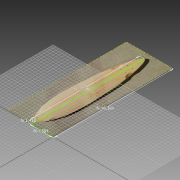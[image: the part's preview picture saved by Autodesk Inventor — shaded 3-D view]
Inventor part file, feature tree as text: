
AUTODESK INVENTOR PART (.ipt)
format: ipt  version: 2014 (Build 180170000, 170)  size: 103,424 bytes
history: native  units: in
note: dims shown in document units (in); Inventor stores cm internally (conversion verified against a paired STEP export)
features: sketch x1, other x1
ambient origin geometry x8: Origin, YZ Plane, XZ Plane, XY Plane, X Axis, Y Axis, Z Axis, Center Point
feature tree (2):
  sketch  "Sketch2"  dims[d1=37.0017in d5=40.3842in d7=7.5541in d8=1.4135in]
  other  "Image1"
